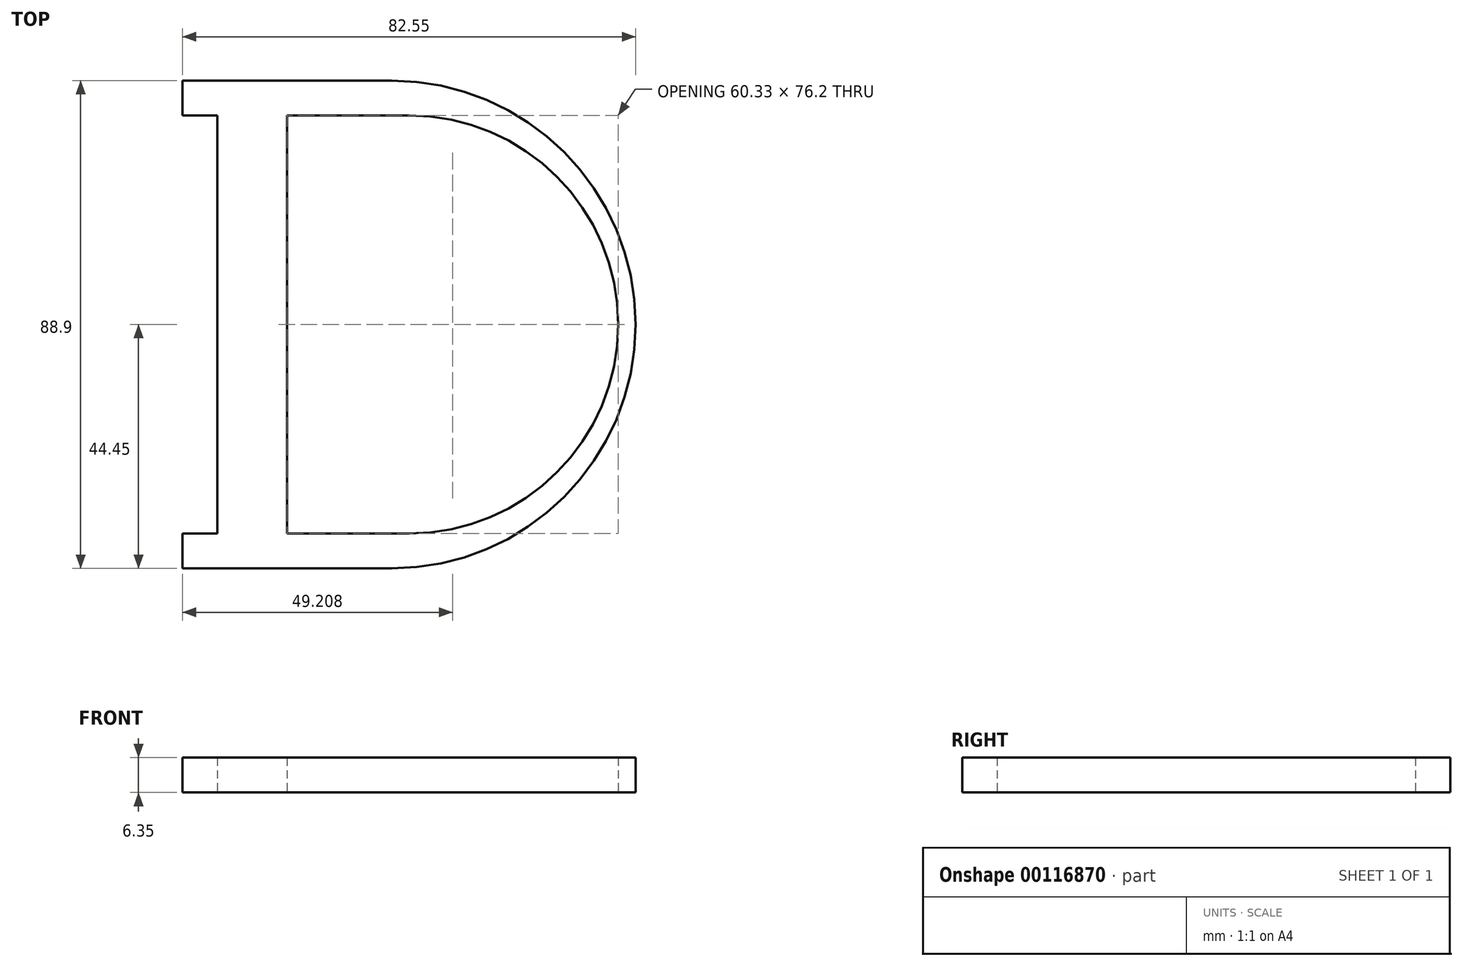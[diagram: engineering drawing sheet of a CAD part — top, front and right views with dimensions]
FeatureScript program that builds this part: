
annotation { "Feature Type Name" : "Feature", "Feature Type Description" : "" }
export const myFeature = defineFeature(function(context is Context, id is Id, definition is map)
    precondition{}
    {
        {
            var Q0;
            Q0=qCreatedBy(makeId("Top.planeOp"),FACE);
            var sketch = newSketch(context, id + "F0", { "sketchPlane" : qUnion([Q0])});
            skLineSegment(sketch, "E0.bottom", {"start": v(41.28, 44.45) * mm, "end": v(-41.27, 44.45) * mm});
            skLineSegment(sketch, "E0.top", {"start": v(41.27, -44.45) * mm, "end": v(-41.28, -44.45) * mm});
            skLineSegment(sketch, "E0.left", {"start": v(41.28, 44.45) * mm, "end": v(41.27, -44.45) * mm});
            skLineSegment(sketch, "E0.right", {"start": v(-41.27, 44.45) * mm, "end": v(-41.27, 38.1) * mm});
            skPoint(sketch, "E0.middle", {"position": v(0, 0) * mm});
            skPoint(sketch, "E1", {"position": v(-41.28, 38.1) * mm});
            skPoint(sketch, "E2", {"position": v(-41.28, -38.1) * mm});
            skLineSegment(sketch, "E3", {"start": v(-41.28, 38.1) * mm, "end": v(-34.92, 38.1) * mm});
            skLineSegment(sketch, "E4.MirrorCS", {"start": v(-41.28, -38.1) * mm, "end": v(-34.92, -38.1) * mm});
            skLineSegment(sketch, "E5", {"start": v(-34.92, 38.1) * mm, "end": v(-34.92, -38.1) * mm});
            skLineSegment(sketch, "E6.trimOffspring", {"start": v(-41.28, -38.1) * mm, "end": v(-41.28, -44.45) * mm});
            skLineSegment(sketch, "E7", {"start": v(-22.22, -38.1) * mm, "end": v(0, -38.1) * mm});
            skArc(sketch, "E8", {"start": v(0, -38.1) * mm, "mid": v(38.1, 0) * mm, "end": v(0, 38.1) * mm});
            skLineSegment(sketch, "E9", {"start": v(0, 38.1) * mm, "end": v(-22.22, 38.1) * mm});
            skLineSegment(sketch, "E10", {"start": v(-22.22, 38.1) * mm, "end": v(-22.22, -38.1) * mm});
            skSolve(sketch);
        }
        {
            var Q0;
            Q0 = qSketchRegion(id + "F0", true);
            extrude(context, id + "F1", {"entities" : qUnion([Q0]), "depth" : 6.35 * mm});
        }
        {
            var Q0;
            Q0=makeQuery(id+"F1.opExtrude","SWEPT_EDGE",EDGE,{"disambiguationData":[OSD([sQuery(id+"F0.wireOp",EDGE,"E0.top"),sQuery(id+"F0.wireOp",EDGE,"E0.left")])]});
            var Q1;
            Q1=makeQuery(id+"F1.opExtrude","SWEPT_EDGE",EDGE,{"disambiguationData":[OSD([sQuery(id+"F0.wireOp",EDGE,"E0.bottom"),sQuery(id+"F0.wireOp",EDGE,"E0.left")])]});
            fillet(context, id + "F2", {"entities" : qUnion([Q0, Q1]), "radius" : 44.45 * mm, "tangentPropagation" : true, "allowEdgeOverflow" : false});
        }
    });
